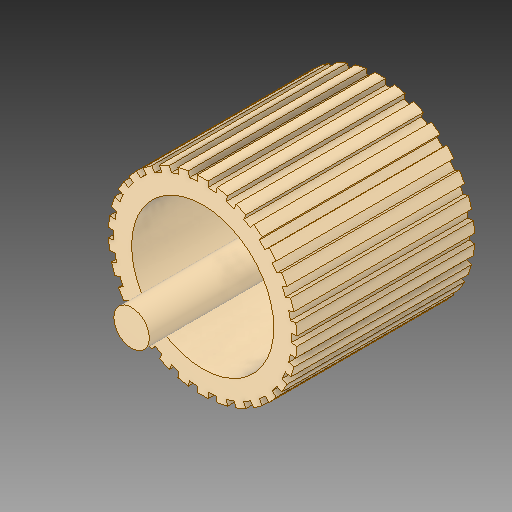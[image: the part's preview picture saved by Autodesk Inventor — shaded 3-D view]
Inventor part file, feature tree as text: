
AUTODESK INVENTOR PART (.ipt)
format: ipt  version: 2018.1 (Build 221171000, 171)  size: 354,304 bytes
history: native  units: mm
features: extrude x3, sketch x3, other x1
ambient origin geometry x8: Origin, YZ Plane, XZ Plane, XY Plane, X Axis, Y Axis, Z Axis, Center Point
bodies: Body1 (feature_tree)
feature tree (7):
  other  "ソリッド1"
  extrude  "押し出し1"  Depth=50.0mm
  extrude  "押し出し2"  Depth=3.0mm
  extrude  "押し出し3"  Depth=3.0mm
  sketch  "スケッチ1"
  sketch  "スケッチ2"
  sketch  "スケッチ3"
